# Revit family: Justerbar Lab Pendle_Bole_Cage
name_source: partatom
category: Lighting Fixtures
units: mm (PartAtom-declared; Revit-internal decimal feet)

## family parameters
Always vertical = Yes
Cut with Voids When Loaded = No
Light Source = Yes
OmniClass Number = 23.80.70.00
OmniClass Title = Lighting
Part Type = Normal
Room Calculation Point = No
Round Connector Dimension = Use Diameter
Shared = No
Work Plane-Based = No

## types (1)
- Justerbar Lab Pendle_Bole_Cage
    Beskyttelsesgrad = IP20
    CRI = >90
    Color Filter = 16777215
    Default Elevation = 0 mm  [stored 0 ft]
    Dimbar = Dali eller Triac
    Dimming Lamp Color Temperature Shift = <None>
    Driftspenning = 220-240V
    Effekt = 6W
    Farger = Sort
    Fargetemperatur = 2700K, 3000K,eller DW
    Frekvens = 50-60 Hz
    Frekvens Sekundærkilde = > 1000 Hz
    Kjøle metode = Passiv
    Levetid = L70 50.000 timer
    Light Source Symbol Size = 610 mm
    Lumen = 660lm
    Lyskilde = LED
    MacAdams = < 3 SCDM
    Pendle Wire = 3360 mm
    Spredning = 120

note: [stored X ft] marks values corroborated as IEEE doubles in the binary element streams (Revit-internal decimal feet)

## geometry (parser evidence)
native form markers: Sweep x14
no freeform markers — native parametric forms only
